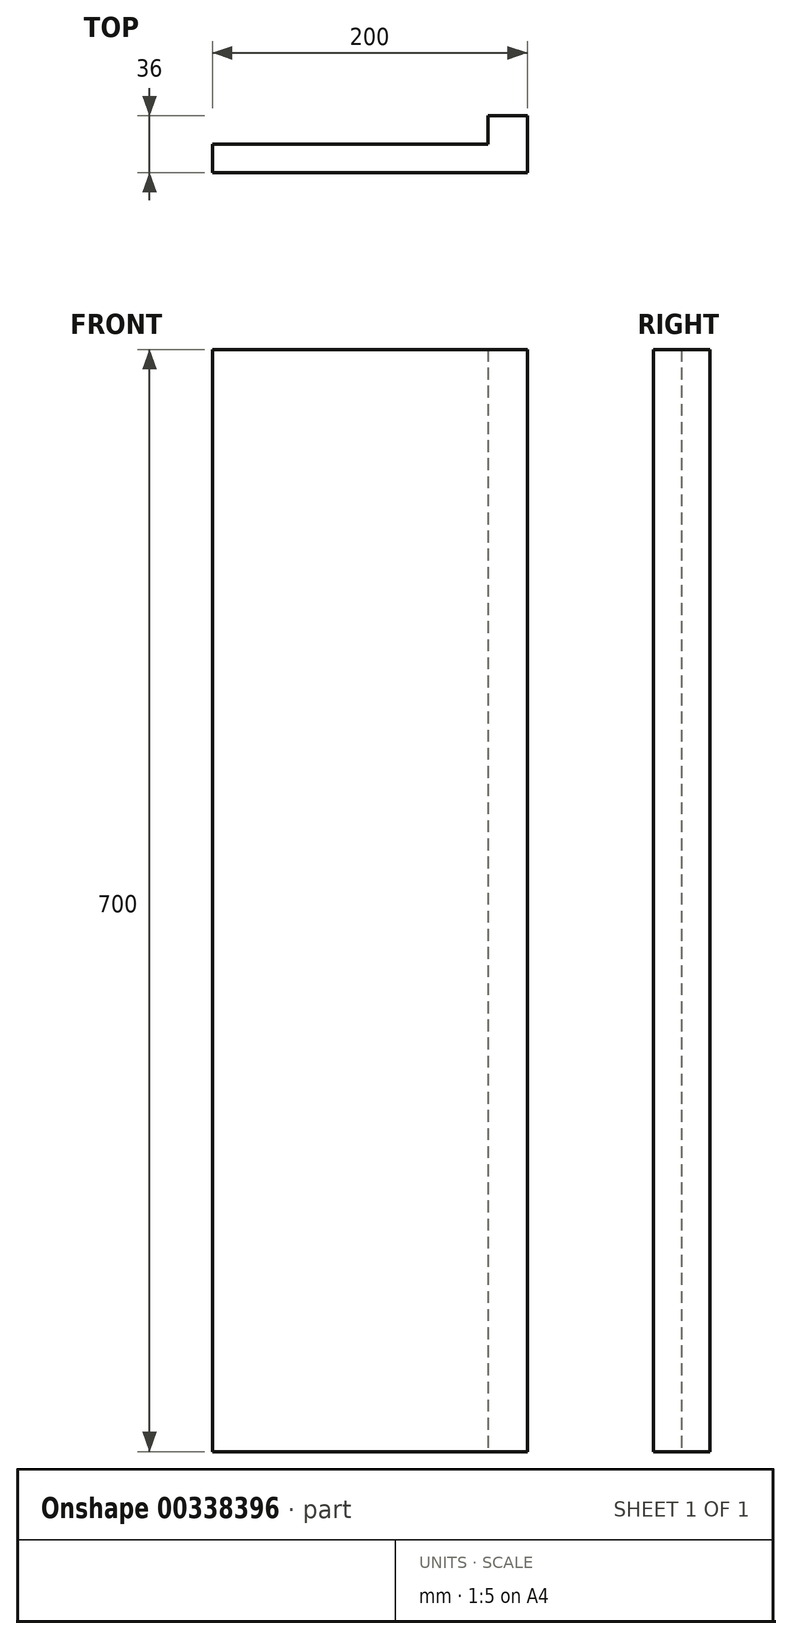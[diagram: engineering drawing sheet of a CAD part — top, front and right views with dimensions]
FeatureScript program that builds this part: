
annotation { "Feature Type Name" : "Feature", "Feature Type Description" : "" }
export const myFeature = defineFeature(function(context is Context, id is Id, definition is map)
    precondition{}
    {
        {
            var Q0;
            Q0=qCreatedBy(makeId("Top.planeOp"),FACE);
            var sketch = newSketch(context, id + "F0", { "sketchPlane" : qUnion([Q0])});
            skLineSegment(sketch, "E0.bottom", {"start": v(-100, -9) * mm, "end": v(100, -9) * mm});
            skLineSegment(sketch, "E0.top", {"start": v(-100, 9) * mm, "end": v(100, 9) * mm});
            skLineSegment(sketch, "E0.left", {"start": v(-100, -9) * mm, "end": v(-100, 9) * mm});
            skLineSegment(sketch, "E0.right", {"start": v(100, -9) * mm, "end": v(100, 9) * mm});
            skPoint(sketch, "E0.middle", {"position": v(0, 0) * mm});
            skLineSegment(sketch, "E1.bottom", {"start": v(100, 9) * mm, "end": v(75, 9) * mm});
            skLineSegment(sketch, "E1.top", {"start": v(100, 27) * mm, "end": v(75, 27) * mm});
            skLineSegment(sketch, "E1.left", {"start": v(100, 9) * mm, "end": v(100, 27) * mm});
            skLineSegment(sketch, "E1.right", {"start": v(75, 9) * mm, "end": v(75, 27) * mm});
            skSolve(sketch);
        }
        {
            var Q0;
            Q0 = qSketchRegion(id + "F0", true);
            extrude(context, id + "F1", {"entities" : qUnion([Q0]), "depth" : 700 * mm, "offsetDistance" : 25 * mm});
        }
    });
